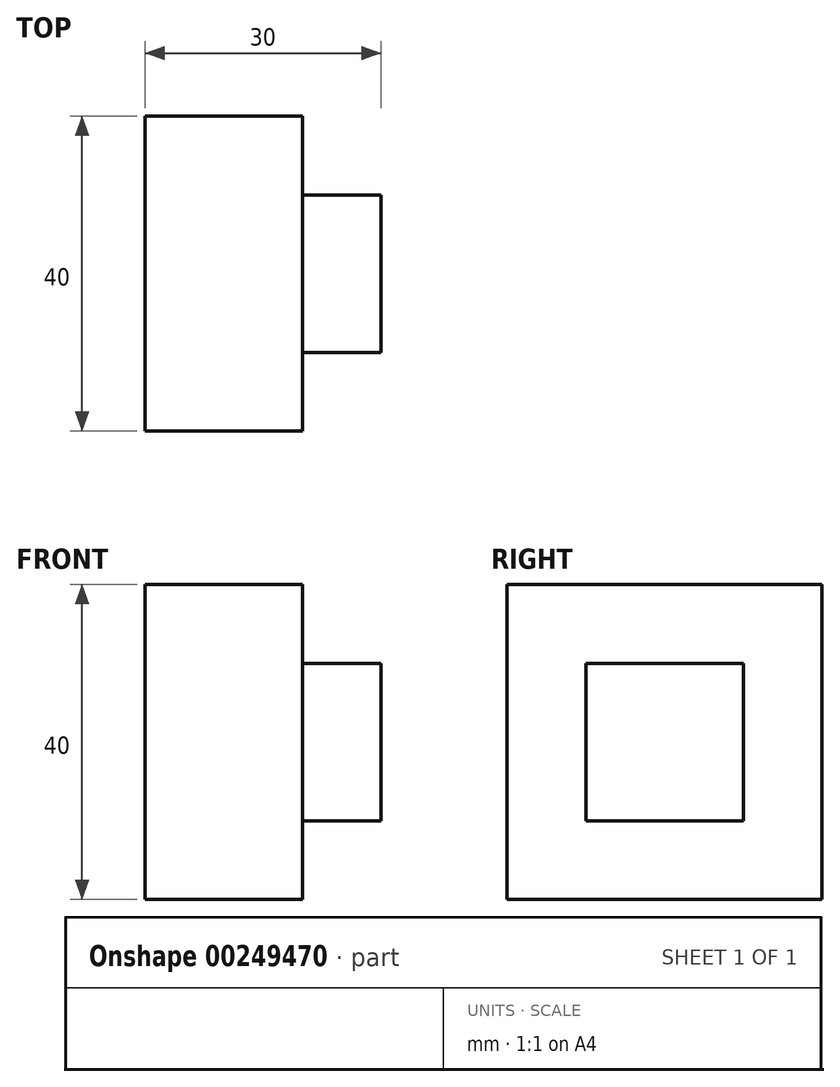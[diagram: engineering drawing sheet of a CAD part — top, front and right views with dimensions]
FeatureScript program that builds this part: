
annotation { "Feature Type Name" : "Feature", "Feature Type Description" : "" }
export const myFeature = defineFeature(function(context is Context, id is Id, definition is map)
    precondition{}
    {
        {
            var Q0;
            Q0=qCreatedBy(makeId("Right.planeOp"),FACE);
            var sketch = newSketch(context, id + "F0", { "sketchPlane" : qUnion([Q0])});
            skLineSegment(sketch, "E0.bottom", {"start": v(20, -20) * mm, "end": v(-20, -20) * mm});
            skLineSegment(sketch, "E0.top", {"start": v(20, 20) * mm, "end": v(-20, 20) * mm});
            skLineSegment(sketch, "E0.left", {"start": v(20, -20) * mm, "end": v(20, 20) * mm});
            skLineSegment(sketch, "E0.right", {"start": v(-20, -20) * mm, "end": v(-20, 20) * mm});
            skSolve(sketch);
        }
        {
            var Q0;
            Q0 = qSketchRegion(id + "F0", true);
            extrude(context, id + "F1", {"entities" : qUnion([Q0]), "depth" : 20 * mm});
        }
        {
            var Q0;
            Q0=makeQuery(id+"F1.opExtrude","CAP_FACE",FACE,{"disambiguationData":[OSD([sQuery(id+"F0.wireOp",EDGE,"E0.bottom"),sQuery(id+"F0.wireOp",EDGE,"E0.top"),sQuery(id+"F0.wireOp",EDGE,"E0.left"),sQuery(id+"F0.wireOp",EDGE,"E0.right")])],"isStart":false});
            var sketch = newSketch(context, id + "F2", { "sketchPlane" : qUnion([Q0])});
            skLineSegment(sketch, "E1.bottom", {"start": v(10, -10) * mm, "end": v(-10, -10) * mm});
            skLineSegment(sketch, "E1.top", {"start": v(10, 10) * mm, "end": v(-10, 10) * mm});
            skLineSegment(sketch, "E1.left", {"start": v(10, -10) * mm, "end": v(10, 10) * mm});
            skLineSegment(sketch, "E1.right", {"start": v(-10, -10) * mm, "end": v(-10, 10) * mm});
            skPoint(sketch, "E1.middle", {"position": v(0, 0) * mm});
            skSolve(sketch);
        }
        {
            var Q0;
            Q0=makeQuery(id+"F2.imprint","IMPRINT",FACE,{"disambiguationData":[TD([[makeQuery(id+"F2.imprint","IMPRINT",EDGE,{"derivedFrom":sQuery(id+"F2.wireOp",EDGE,"E1.bottom")}),-1.0]])]});
            extrude(context, id + "F3", {"entities" : qUnion([Q0]), "operationType" : NewBodyOperationType.ADD, "depth" : 10 * mm});
        }
    });
